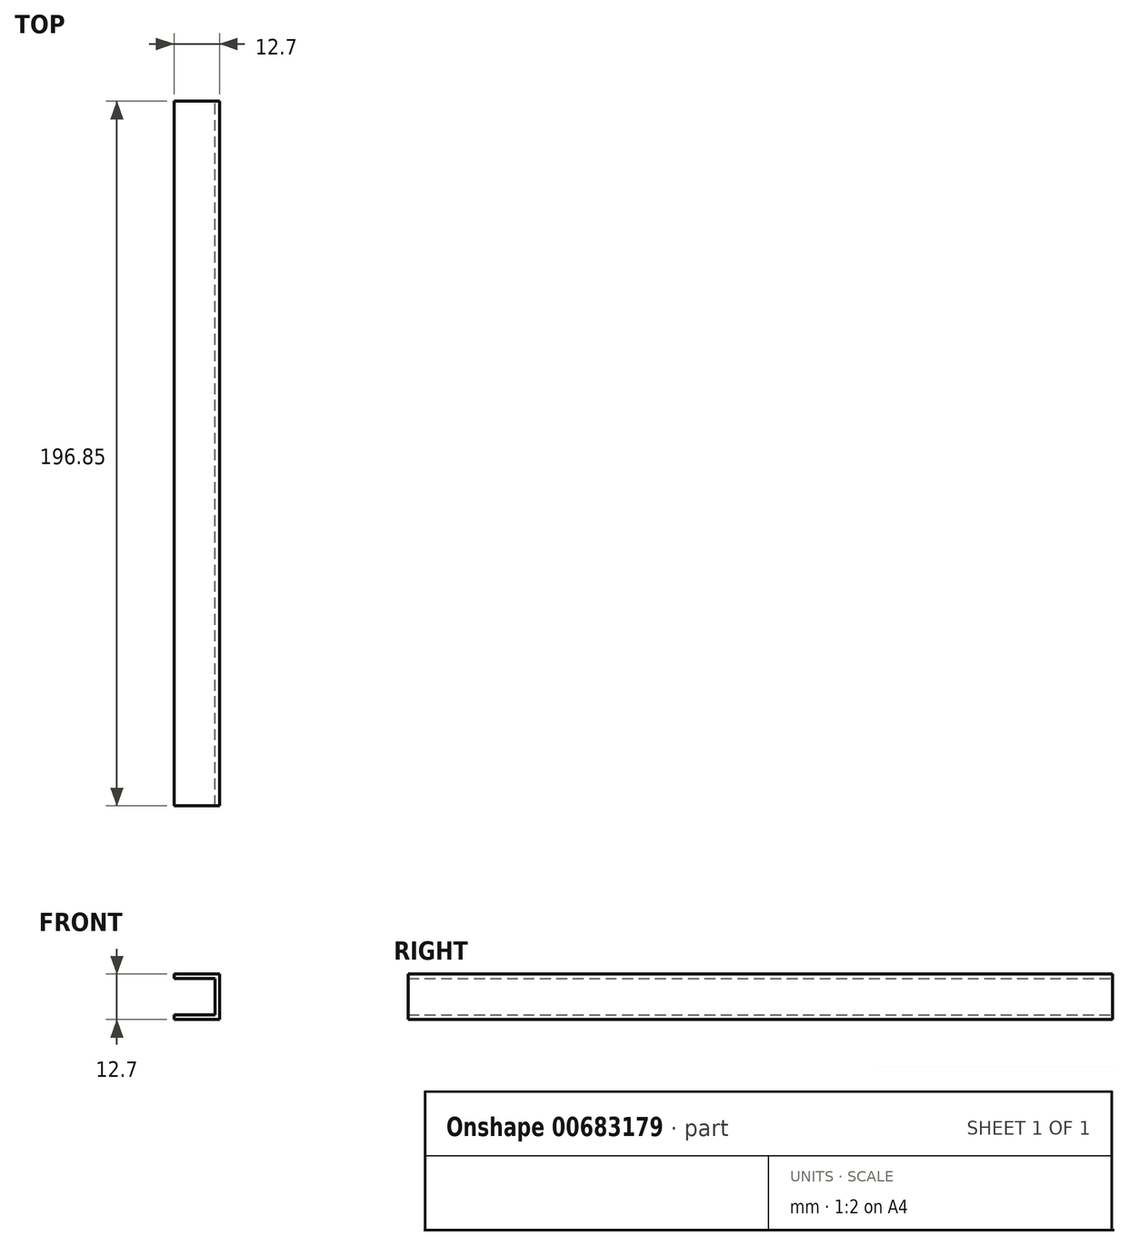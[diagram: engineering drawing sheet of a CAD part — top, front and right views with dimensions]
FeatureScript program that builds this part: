
annotation { "Feature Type Name" : "Feature", "Feature Type Description" : "" }
export const myFeature = defineFeature(function(context is Context, id is Id, definition is map)
    precondition{}
    {
        {
            var Q0;
            Q0=qCreatedBy(makeId("Front.planeOp"),FACE);
            var sketch = newSketch(context, id + "F0", { "sketchPlane" : qUnion([Q0])});
            skLineSegment(sketch, "E0", {"start": v(0, 12.7) * mm, "end": v(12.7, 12.7) * mm});
            skLineSegment(sketch, "E1", {"start": v(12.7, 12.7) * mm, "end": v(12.7, 0) * mm});
            skLineSegment(sketch, "E2", {"start": v(12.7, 0) * mm, "end": v(0, 0) * mm});
            skLineSegment(sketch, "E3", {"start": v(0, 0) * mm, "end": v(0, 1.27) * mm});
            skLineSegment(sketch, "E4", {"start": v(0, 1.27) * mm, "end": v(11.43, 1.27) * mm});
            skLineSegment(sketch, "E5", {"start": v(11.43, 1.27) * mm, "end": v(11.43, 11.43) * mm});
            skLineSegment(sketch, "E6", {"start": v(11.43, 11.43) * mm, "end": v(0, 11.43) * mm});
            skLineSegment(sketch, "E7", {"start": v(0, 11.43) * mm, "end": v(0, 12.7) * mm});
            skSolve(sketch);
        }
        {
            var Q0;
            Q0=makeQuery(id+"F0.imprint","IMPRINT",FACE,{"disambiguationData":[TD([[makeQuery(id+"F0.imprint","IMPRINT",EDGE,{"derivedFrom":sQuery(id+"F0.wireOp",EDGE,"E0")}),-1.0]])]});
            extrude(context, id + "F1", {"entities" : qUnion([Q0]), "depth" : 196.85 * mm, "offsetDistance" : 25.4 * mm});
        }
    });
